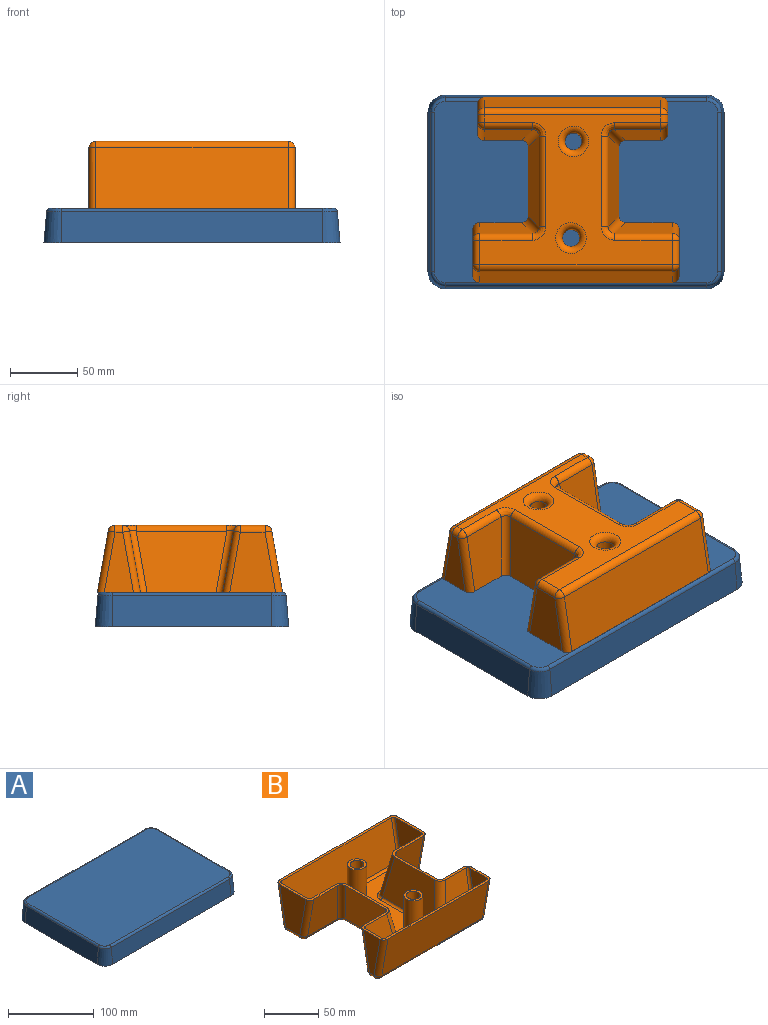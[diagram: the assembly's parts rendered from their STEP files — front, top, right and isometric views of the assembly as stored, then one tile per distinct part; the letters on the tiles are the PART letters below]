
ASSEMBLY  parts=2 mates=1
PART A: 27 faces, bbox 219.9x143.7x25.4 mm
  f0: plane 219.86x143.73mm, normal (0,0,-1), area 1778mm2, adj f1,f2,f3,f4,f5,f6,f7,f8
  f1: plane 194.46x23.08mm, normal (0,1,0.09), area 4505.5mm2, adj f0,f2,f8,f17
  f2: cone r=12.7mm half-angle=5deg, axis (0,0,-1), area 425.5mm2, adj f0,f1,f3,f15
  f3: plane 118.33x23.08mm, normal (-1,0,0.09), area 2741.6mm2, adj f0,f2,f4,f13
  f4: cone r=12.7mm half-angle=5deg, axis (0,0,-1), area 425.5mm2, adj f0,f3,f5,f11
  f5: plane 194.46x23.08mm, normal (0,-1,0.09), area 4505.5mm2, adj f0,f4,f6,f10
  f6: cone r=12.7mm half-angle=5deg, axis (0,0,-1), area 425.5mm2, adj f0,f5,f7,f12
  f7: plane 118.33x23.08mm, normal (1,0,0.09), area 2741.6mm2, adj f0,f6,f8,f14
  f8: cone r=12.7mm half-angle=5deg, axis (0,0,-1), area 425.5mm2, adj f0,f1,f7,f16
  f9: plane 210.76x134.63mm, normal (0,0,1), area 28316.9mm2, adj f10,f11,f12,f13,f14,f15,f16,f17
  f10: cylinder r=2.54mm len=194.46mm, axis (1,0,0), area 732.7mm2, adj f5,f9,f11,f12
  f11: torus R=8.15mm, axis (0,0,1), area 57.5mm2, adj f4,f9,f10,f13
  f12: torus R=8.15mm, axis (0,0,1), area 57.5mm2, adj f6,f9,f10,f14
  f13: cylinder r=2.54mm len=118.33mm, axis (0,1,0), area 445.9mm2, adj f3,f9,f11,f15
  f14: cylinder r=2.54mm len=118.33mm, axis (0,1,0), area 445.9mm2, adj f7,f9,f12,f16
  f15: torus R=8.15mm, axis (0,0,1), area 57.5mm2, adj f2,f9,f13,f17
  f16: torus R=8.15mm, axis (0,0,1), area 57.5mm2, adj f8,f9,f14,f17
  f17: cylinder r=2.54mm len=194.46mm, axis (1,0,0), area 732.7mm2, adj f1,f9,f15,f16
  f18: plane 194.46x22.86mm, normal (0,-1,-0.09), area 4462.3mm2, adj f0,f19,f25,f26
  f19: cone r=10.17mm half-angle=5deg, axis (0,0,-1), area 329.8mm2, adj f0,f18,f20,f26
  f20: plane 118.33x22.86mm, normal (1,0,-0.09), area 2715.3mm2, adj f0,f19,f21,f26
  f21: cone r=10.17mm half-angle=5deg, axis (0,0,-1), area 329.8mm2, adj f0,f20,f22,f26
  f22: plane 194.46x22.86mm, normal (0,1,-0.09), area 4462.3mm2, adj f0,f21,f23,f26
  f23: cone r=10.17mm half-angle=5deg, axis (0,0,-1), area 329.8mm2, adj f0,f22,f24,f26
  f24: plane 118.33x22.86mm, normal (-1,0,-0.09), area 2715.3mm2, adj f0,f23,f25,f26
  f25: cone r=10.17mm half-angle=5deg, axis (0,0,-1), area 329.8mm2, adj f0,f18,f24,f26
  f26: plane 210.76x134.63mm, normal (0,0,-1), area 28316.9mm2, adj f18,f19,f20,f21,f22,f23,f24,f25
PART B: 109 faces, bbox 153.4x137.8x50.9 mm
  f0: plane 17.78x17.78mm, normal (0,0,1), area 121.6mm2, adj f53,f106
  f1: plane 153.42x137.8mm, normal (0,0,1), area 1790.1mm2, adj f3,f4,f5,f6,f7,f8,f9,f10
  f2: plane 143.07x111.53mm, normal (0,0,-1), area 6252.5mm2, adj f17,f19,f22,f23,f25,f28,f29,f34
  f3: plane 44.7x34.18mm, normal (1,0,0), area 1175.5mm2, adj f1,f18,f23,f24
  f4: plane 143.07x45.59mm, normal (0,0.98,-0.17), area 6622.7mm2, adj f1,f24,f29,f30
  f5: plane 44.7x34.18mm, normal (-1,0,0), area 1175.5mm2, adj f1,f30,f35,f36
  f6: plane 45.59x39.21mm, normal (0,-0.98,-0.17), area 1628.8mm2, adj f1,f36,f41,f42
  f7: plane 67.23x45.59mm, normal (-0.98,0,-0.17), area 2739.8mm2, adj f1,f42,f47,f48
  f8: plane 45.59x35.67mm, normal (0,0.98,-0.17), area 1465mm2, adj f1,f45,f48,f51
  f9: plane 44.7x21.64mm, normal (-1,0,0), area 615.2mm2, adj f1,f39,f45,f46
  f10: plane 131.05x45.59mm, normal (0,-0.98,-0.17), area 6066.4mm2, adj f1,f33,f39,f40
  f11: plane 44.7x21.64mm, normal (1,0,0), area 615.2mm2, adj f1,f27,f33,f34
  f12: plane 45.59x34.3mm, normal (0,0.98,-0.17), area 1401.5mm2, adj f1,f21,f27,f28
  f13: plane 67.23x45.59mm, normal (0.98,0,-0.17), area 2739.8mm2, adj f1,f16,f21,f22
  f14: plane 45.59x42.78mm, normal (0,-0.98,-0.17), area 1794mm2, adj f1,f16,f17,f18
  f15: plane 17.78x17.78mm, normal (0,0,1), area 121.6mm2, adj f52,f105
  f16: cylinder r=5.08mm len=46.63mm, axis (0.17,-0.17,0.97), area 369.5mm2, adj f1,f13,f14,f19
  f17: cylinder r=5.08mm len=42.78mm, axis (-1,0,0), area 303.4mm2, adj f2,f14,f19,f20
  f18: cylinder r=5.08mm len=46.47mm, axis (0,0.17,-0.98), area 366.8mm2, adj f1,f3,f14,f20
  f19: bspline ~10.01x10.01mm, area 76.3mm2, adj f2,f16,f17,f22
  f20: sphere r=5.08mm, area 36mm2, adj f17,f18,f23
  f21: cylinder r=5.08mm len=46.63mm, axis (0.17,0.17,0.97), area 369.5mm2, adj f1,f12,f13,f25
  f22: cylinder r=5.08mm len=67.23mm, axis (0,-1,0), area 476.8mm2, adj f2,f13,f19,f25
  f23: cylinder r=5.08mm len=18.41mm, axis (0,1,0), area 146.9mm2, adj f2,f3,f20,f26
  f24: cylinder r=5.08mm len=46.47mm, axis (0,-0.17,-0.98), area 366.8mm2, adj f1,f3,f4,f26
  f25: bspline ~10.01x10.01mm, area 76.3mm2, adj f2,f21,f22,f28
  f26: sphere r=5.08mm, area 36mm2, adj f23,f24,f29
  f27: cylinder r=5.08mm len=46.47mm, axis (0,0.17,0.98), area 366.8mm2, adj f1,f11,f12,f31
  f28: cylinder r=5.08mm len=34.3mm, axis (-1,0,0), area 243.3mm2, adj f2,f12,f25,f31
  f29: cylinder r=5.08mm len=143.07mm, axis (-1,0,0), area 1014.8mm2, adj f2,f4,f26,f32
  f30: cylinder r=5.08mm len=46.47mm, axis (0,0.17,0.98), area 366.8mm2, adj f1,f4,f5,f32
  f31: sphere r=5.08mm, area 36mm2, adj f27,f28,f34
  f32: sphere r=5.08mm, area 36mm2, adj f29,f30,f35
  f33: cylinder r=5.08mm len=46.47mm, axis (0,-0.17,0.98), area 366.8mm2, adj f1,f10,f11,f37
  f34: cylinder r=5.08mm len=5.88mm, axis (0,1,0), area 46.9mm2, adj f2,f11,f31,f37
  f35: cylinder r=5.08mm len=18.41mm, axis (0,-1,0), area 146.9mm2, adj f2,f5,f32,f38
  f36: cylinder r=5.08mm len=46.47mm, axis (0,-0.17,0.98), area 366.8mm2, adj f1,f5,f6,f38
  f37: sphere r=5.08mm, area 36mm2, adj f33,f34,f40
  f38: sphere r=5.08mm, area 36mm2, adj f35,f36,f41
  f39: cylinder r=5.08mm len=46.47mm, axis (0,0.17,-0.98), area 366.8mm2, adj f1,f9,f10,f43
  f40: cylinder r=5.08mm len=131.05mm, axis (-1,0,0), area 929.6mm2, adj f2,f10,f37,f43
  f41: cylinder r=5.08mm len=39.21mm, axis (-1,0,0), area 278.1mm2, adj f2,f6,f38,f44
  f42: cylinder r=5.08mm len=46.63mm, axis (-0.17,-0.17,0.97), area 369.5mm2, adj f1,f6,f7,f44
  f43: sphere r=5.08mm, area 36mm2, adj f39,f40,f46
  f44: bspline ~10.01x10.01mm, area 76.3mm2, adj f2,f41,f42,f47
  f45: cylinder r=5.08mm len=46.47mm, axis (0,-0.17,-0.98), area 366.8mm2, adj f1,f8,f9,f49
  f46: cylinder r=5.08mm len=5.88mm, axis (0,-1,0), area 46.9mm2, adj f2,f9,f43,f49
  f47: cylinder r=5.08mm len=67.23mm, axis (0,-1,0), area 476.8mm2, adj f2,f7,f44,f50
  f48: cylinder r=5.08mm len=46.63mm, axis (-0.17,0.17,0.97), area 369.5mm2, adj f1,f7,f8,f50
  f49: sphere r=5.08mm, area 36mm2, adj f45,f46,f51
  f50: bspline ~10.01x10.01mm, area 76.3mm2, adj f2,f47,f48,f51
  f51: cylinder r=5.08mm len=35.67mm, axis (-1,0,0), area 253mm2, adj f2,f8,f49,f50
  f52: cylinder r=6.35mm len=44.7mm, axis (0,0,-1), area 1783.6mm2, adj f15,f55
  f53: cylinder r=6.35mm len=44.7mm, axis (0,0,-1), area 1783.6mm2, adj f0,f54
  f54: torus R=11.43mm, axis (0,0,1), area 410.9mm2, adj f2,f53
  f55: torus R=11.43mm, axis (0,0,1), area 410.9mm2, adj f2,f52
  f56: plane 143.07x111.53mm, normal (0,0,1), area 6252.5mm2, adj f70,f72,f75,f76,f78,f81,f82,f87
  f57: plane 44.7x34.18mm, normal (-1,0,0), area 1175.5mm2, adj f1,f71,f76,f77
  f58: plane 143.07x45.15mm, normal (0,-0.98,0.17), area 6558.6mm2, adj f1,f77,f82,f83
  f59: plane 44.7x34.18mm, normal (1,0,0), area 1175.5mm2, adj f1,f83,f88,f89
  f60: plane 45.15x39.21mm, normal (0,0.98,0.17), area 1614.8mm2, adj f1,f89,f94,f95
  f61: plane 67.23x45.15mm, normal (0.98,0,0.17), area 2716.8mm2, adj f1,f95,f100,f101
  f62: plane 45.15x35.67mm, normal (0,-0.98,0.17), area 1452.6mm2, adj f1,f98,f101,f104
  f63: plane 44.7x21.64mm, normal (1,0,0), area 615.2mm2, adj f1,f92,f98,f99
  f64: plane 131.05x45.15mm, normal (0,0.98,0.17), area 6007.7mm2, adj f1,f86,f92,f93
  f65: plane 44.7x21.64mm, normal (-1,0,0), area 615.2mm2, adj f1,f80,f86,f87
  f66: plane 45.15x34.3mm, normal (0,-0.98,0.17), area 1389.7mm2, adj f1,f74,f80,f81
  f67: plane 67.23x45.15mm, normal (-0.98,0,0.17), area 2716.8mm2, adj f1,f69,f74,f75
  f68: plane 45.15x42.78mm, normal (0,0.98,0.17), area 1778.4mm2, adj f1,f69,f70,f71
  f69: cylinder r=7.62mm len=46.36mm, axis (0.17,-0.17,0.97), area 547.6mm2, adj f1,f67,f68,f72
  f70: cylinder r=2.54mm len=42.78mm, axis (-1,0,0), area 151.7mm2, adj f56,f68,f72,f73
  f71: cylinder r=2.54mm len=45.59mm, axis (0,0.17,-0.98), area 182mm2, adj f1,f57,f68,f73
  f72: bspline ~10.01x10.01mm, area 46.1mm2, adj f56,f69,f70,f75
  f73: sphere r=2.54mm, area 9mm2, adj f70,f71,f76
  f74: cylinder r=7.62mm len=46.36mm, axis (0.17,0.17,0.97), area 547.6mm2, adj f1,f66,f67,f78
  f75: cylinder r=2.54mm len=67.23mm, axis (0,-1,0), area 238.4mm2, adj f56,f67,f72,f78
  f76: cylinder r=2.54mm len=18.41mm, axis (0,1,0), area 73.5mm2, adj f56,f57,f73,f79
  f77: cylinder r=2.54mm len=45.59mm, axis (0,-0.17,-0.98), area 182mm2, adj f1,f57,f58,f79
  f78: bspline ~10.01x10.01mm, area 46.1mm2, adj f56,f74,f75,f81
  f79: sphere r=2.54mm, area 9.3mm2, adj f76,f77,f82
  f80: cylinder r=2.54mm len=45.59mm, axis (0,0.17,0.98), area 182mm2, adj f1,f65,f66,f84
  f81: cylinder r=2.54mm len=34.3mm, axis (-1,0,0), area 121.6mm2, adj f56,f66,f78,f84
  f82: cylinder r=2.54mm len=143.07mm, axis (-1,0,0), area 507.4mm2, adj f56,f58,f79,f85
  f83: cylinder r=2.54mm len=45.59mm, axis (0,0.17,0.98), area 182mm2, adj f1,f58,f59,f85
  f84: sphere r=2.54mm, area 9.3mm2, adj f80,f81,f87
  f85: sphere r=2.54mm, area 9.3mm2, adj f82,f83,f88
  f86: cylinder r=2.54mm len=45.59mm, axis (0,-0.17,0.98), area 182mm2, adj f1,f64,f65,f90
  f87: cylinder r=2.54mm len=5.88mm, axis (0,1,0), area 23.5mm2, adj f56,f65,f84,f90
  f88: cylinder r=2.54mm len=18.41mm, axis (0,-1,0), area 73.5mm2, adj f56,f59,f85,f91
  f89: cylinder r=2.54mm len=45.59mm, axis (0,-0.17,0.98), area 182mm2, adj f1,f59,f60,f91
  f90: sphere r=2.54mm, area 9mm2, adj f86,f87,f93
  f91: sphere r=2.54mm, area 9.3mm2, adj f88,f89,f94
  f92: cylinder r=2.54mm len=45.59mm, axis (0,0.17,-0.98), area 182mm2, adj f1,f63,f64,f96
  f93: cylinder r=2.54mm len=131.05mm, axis (-1,0,0), area 464.8mm2, adj f56,f64,f90,f96
  f94: cylinder r=2.54mm len=39.21mm, axis (-1,0,0), area 139mm2, adj f56,f60,f91,f97
  f95: cylinder r=7.62mm len=46.36mm, axis (-0.17,-0.17,0.97), area 547.6mm2, adj f1,f60,f61,f97
  f96: sphere r=2.54mm, area 9.3mm2, adj f92,f93,f99
  f97: bspline ~10.01x10.01mm, area 46.1mm2, adj f56,f94,f95,f100
  f98: cylinder r=2.54mm len=45.59mm, axis (0,-0.17,-0.98), area 182mm2, adj f1,f62,f63,f102
  f99: cylinder r=2.54mm len=5.88mm, axis (0,-1,0), area 23.5mm2, adj f56,f63,f96,f102
  f100: cylinder r=2.54mm len=67.23mm, axis (0,-1,0), area 238.4mm2, adj f56,f61,f97,f103
  f101: cylinder r=7.62mm len=46.36mm, axis (-0.17,0.17,0.97), area 547.6mm2, adj f1,f61,f62,f103
  f102: sphere r=2.54mm, area 9.3mm2, adj f98,f99,f104
  f103: bspline ~10.01x10.01mm, area 46.1mm2, adj f56,f100,f101,f104
  f104: cylinder r=2.54mm len=35.67mm, axis (-1,0,0), area 126.5mm2, adj f56,f62,f102,f103
  f105: cylinder r=8.89mm len=44.7mm, axis (0,0,-1), area 2497.1mm2, adj f15,f108
  f106: cylinder r=8.89mm len=44.7mm, axis (0,0,-1), area 2497.1mm2, adj f0,f107
  f107: torus R=11.43mm, axis (0,0,1), area 246mm2, adj f56,f106
  f108: torus R=11.43mm, axis (0,0,1), area 246mm2, adj f56,f105
PLACE A rot(axis=(-1,0,0),0deg) t=(-37.12,-19.89,-7.83)mm
PLACE B rot(axis=(1,0,0),180deg) t=(-31.78,-17.14,67.36)mm
MATE planar B.f52 <-> A.f9  axis (0,0,-1) through (-39.11,-58.05,17.57)mm
